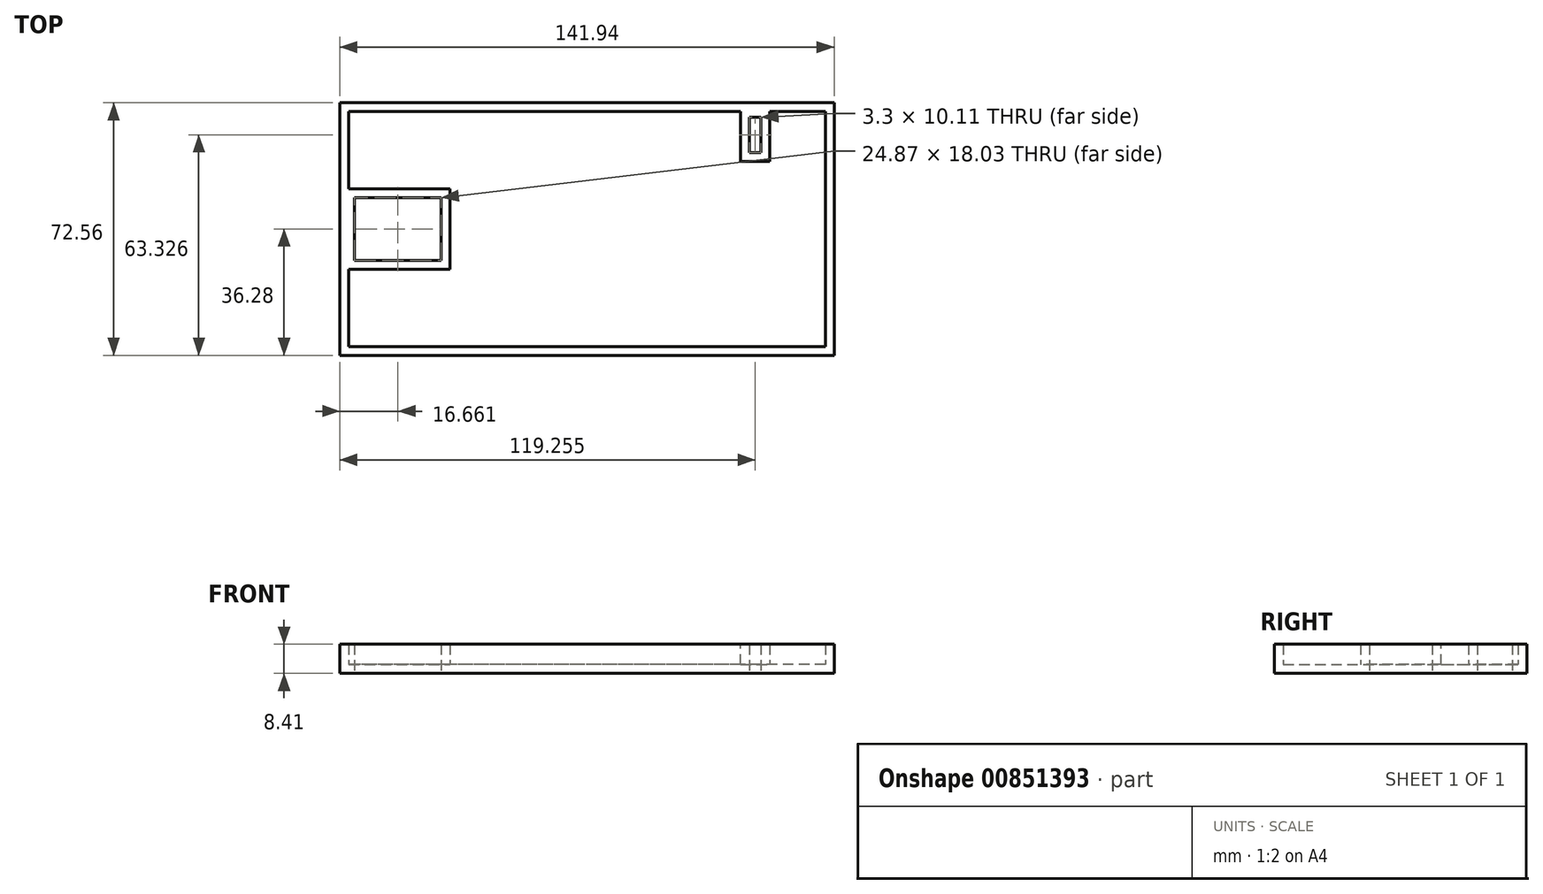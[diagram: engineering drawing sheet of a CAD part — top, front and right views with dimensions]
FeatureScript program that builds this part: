
annotation { "Feature Type Name" : "Feature", "Feature Type Description" : "" }
export const myFeature = defineFeature(function(context is Context, id is Id, definition is map)
    precondition{}
    {
        {
            var Q0;
            Q0=qCreatedBy(makeId("Top.planeOp"),FACE);
            var sketch = newSketch(context, id + "F0", { "sketchPlane" : qUnion([Q0])});
            skLineSegment(sketch, "E0.bottom", {"start": v(70.97, -36.28) * mm, "end": v(-70.97, -36.28) * mm});
            skLineSegment(sketch, "E0.top", {"start": v(70.97, 36.28) * mm, "end": v(-70.97, 36.28) * mm});
            skLineSegment(sketch, "E0.left", {"start": v(70.97, -36.28) * mm, "end": v(70.97, 36.28) * mm});
            skLineSegment(sketch, "E0.right", {"start": v(-70.97, -36.28) * mm, "end": v(-70.97, 36.28) * mm});
            skPoint(sketch, "E0.middle", {"position": v(0, 0) * mm});
            skLineSegment(sketch, "E1.bottom", {"start": v(-66.74, 9.02) * mm, "end": v(-41.88, 9.02) * mm});
            skLineSegment(sketch, "E1.top", {"start": v(-66.74, -9.02) * mm, "end": v(-41.88, -9.02) * mm});
            skLineSegment(sketch, "E1.left", {"start": v(-66.74, 9.02) * mm, "end": v(-66.74, -9.02) * mm});
            skLineSegment(sketch, "E1.right", {"start": v(-41.88, 9.02) * mm, "end": v(-41.88, -9.02) * mm});
            skPoint(sketch, "E1.middle", {"position": v(-54.3, 0) * mm});
            skLineSegment(sketch, "E2.bottom", {"start": v(46.63, 32.1) * mm, "end": v(49.94, 32.1) * mm});
            skLineSegment(sketch, "E2.top", {"start": v(46.63, 22) * mm, "end": v(49.94, 22) * mm});
            skLineSegment(sketch, "E2.left", {"start": v(46.63, 32.1) * mm, "end": v(46.63, 22) * mm});
            skLineSegment(sketch, "E2.right", {"start": v(49.94, 32.1) * mm, "end": v(49.94, 22) * mm});
            skSolve(sketch);
        }
        {
            var Q0;
            Q0 = qSketchRegion(id + "F0", true);
            extrude(context, id + "F1", {"entities" : qUnion([Q0]), "depth" : 8.4 * mm, "offsetDistance" : 25.4 * mm});
        }
        {
            var Q0;
            Q0=makeQuery(id+"F1.opExtrude","CAP_FACE",FACE,{"disambiguationData":[OSD([sQuery(id+"F0.wireOp",EDGE,"E0.bottom"),sQuery(id+"F0.wireOp",EDGE,"E0.top"),sQuery(id+"F0.wireOp",EDGE,"E0.left"),sQuery(id+"F0.wireOp",EDGE,"E0.right"),sQuery(id+"F0.wireOp",EDGE,"E1.bottom"),sQuery(id+"F0.wireOp",EDGE,"E1.top"),sQuery(id+"F0.wireOp",EDGE,"E1.left"),sQuery(id+"F0.wireOp",EDGE,"E1.right"),sQuery(id+"F0.wireOp",EDGE,"E2.bottom"),sQuery(id+"F0.wireOp",EDGE,"E2.top"),sQuery(id+"F0.wireOp",EDGE,"E2.left"),sQuery(id+"F0.wireOp",EDGE,"E2.right")])],"isStart":false});
            shell(context, id + "F2", {"entities" : qUnion([Q0]), "thickness" : 2.54 * mm});
        }
    });
